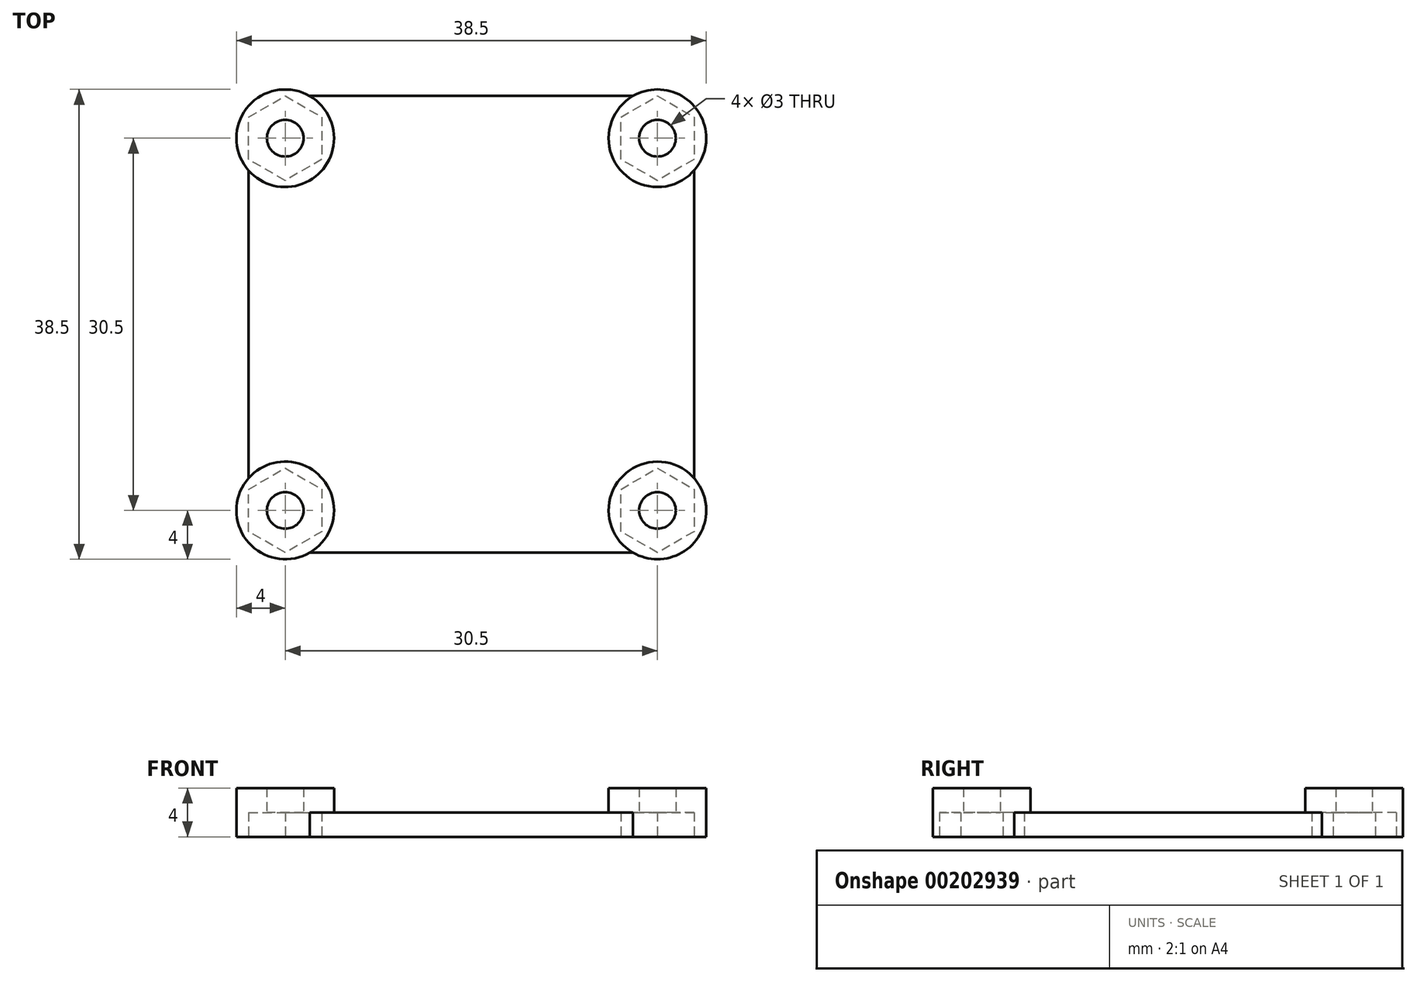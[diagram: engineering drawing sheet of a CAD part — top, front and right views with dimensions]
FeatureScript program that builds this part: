
annotation { "Feature Type Name" : "Feature", "Feature Type Description" : "" }
export const myFeature = defineFeature(function(context is Context, id is Id, definition is map)
    precondition{}
    {
        {
            var Q0;
            Q0=qCreatedBy(makeId("Top.planeOp"),FACE);
            var sketch = newSketch(context, id + "F0", { "sketchPlane" : qUnion([Q0])});
            skCircle(sketch, "E0", {"center": v(0, 0) * mm, "radius": 1.5 * mm});
            skCircle(sketch, "E1.0.1.0", {"center": v(0, 30.5) * mm, "radius": 1.5 * mm});
            skCircle(sketch, "E1.1.0.0", {"center": v(30.5, 0) * mm, "radius": 1.5 * mm});
            skCircle(sketch, "E1.1.1.0", {"center": v(30.5, 30.5) * mm, "radius": 1.5 * mm});
            skLineSegment(sketch, "E1.direction1", {"start": v(0, 0) * mm, "end": v(30.5, 0) * mm, "construction": true});
            skLineSegment(sketch, "E1.direction2", {"start": v(0, 0) * mm, "end": v(0, 30.5) * mm, "construction": true});
            skCircle(sketch, "E2", {"center": v(0, 0) * mm, "radius": 4 * mm});
            skCircle(sketch, "E3.0.1.0", {"center": v(0, 30.5) * mm, "radius": 4 * mm});
            skCircle(sketch, "E3.1.0.0", {"center": v(30.5, 0) * mm, "radius": 4 * mm});
            skCircle(sketch, "E3.1.1.0", {"center": v(30.5, 30.5) * mm, "radius": 4 * mm});
            skCircle(sketch, "E4.cCircle", {"center": v(0, 0) * mm, "radius": 3 * mm});
            skLineSegment(sketch, "E4.0", {"start": v(3, 1.73) * mm, "end": v(3, -1.73) * mm});
            skLineSegment(sketch, "E4.1", {"start": v(3, -1.73) * mm, "end": v(0, -3.46) * mm});
            skLineSegment(sketch, "E4.2", {"start": v(0, -3.46) * mm, "end": v(-3, -1.73) * mm});
            skLineSegment(sketch, "E4.3", {"start": v(-3, -1.73) * mm, "end": v(-3, 1.73) * mm});
            skLineSegment(sketch, "E4.4", {"start": v(-3, 1.73) * mm, "end": v(0, 3.46) * mm});
            skLineSegment(sketch, "E4.5", {"start": v(0, 3.46) * mm, "end": v(3, 1.73) * mm});
            skPoint(sketch, "E4.0.midPoint", {"position": v(3, 0) * mm});
            skLineSegment(sketch, "E5.0.1.0", {"start": v(0, 33.96) * mm, "end": v(3, 32.23) * mm});
            skLineSegment(sketch, "E5.0.1.1", {"start": v(3, 32.23) * mm, "end": v(3, 28.77) * mm});
            skLineSegment(sketch, "E5.0.1.2", {"start": v(3, 28.77) * mm, "end": v(0, 27.04) * mm});
            skLineSegment(sketch, "E5.0.1.3", {"start": v(0, 27.04) * mm, "end": v(-3, 28.77) * mm});
            skLineSegment(sketch, "E5.0.1.4", {"start": v(-3, 28.77) * mm, "end": v(-3, 32.23) * mm});
            skLineSegment(sketch, "E5.0.1.5", {"start": v(-3, 32.23) * mm, "end": v(0, 33.96) * mm});
            skLineSegment(sketch, "E5.1.0.0", {"start": v(30.5, 3.46) * mm, "end": v(33.5, 1.73) * mm});
            skLineSegment(sketch, "E5.1.0.1", {"start": v(33.5, 1.73) * mm, "end": v(33.5, -1.73) * mm});
            skLineSegment(sketch, "E5.1.0.2", {"start": v(33.5, -1.73) * mm, "end": v(30.5, -3.46) * mm});
            skLineSegment(sketch, "E5.1.0.3", {"start": v(30.5, -3.46) * mm, "end": v(27.5, -1.73) * mm});
            skLineSegment(sketch, "E5.1.0.4", {"start": v(27.5, -1.73) * mm, "end": v(27.5, 1.73) * mm});
            skLineSegment(sketch, "E5.1.0.5", {"start": v(27.5, 1.73) * mm, "end": v(30.5, 3.46) * mm});
            skLineSegment(sketch, "E5.1.1.0", {"start": v(30.5, 33.96) * mm, "end": v(33.5, 32.23) * mm});
            skLineSegment(sketch, "E5.1.1.1", {"start": v(33.5, 32.23) * mm, "end": v(33.5, 28.77) * mm});
            skLineSegment(sketch, "E5.1.1.2", {"start": v(33.5, 28.77) * mm, "end": v(30.5, 27.04) * mm});
            skLineSegment(sketch, "E5.1.1.3", {"start": v(30.5, 27.04) * mm, "end": v(27.5, 28.77) * mm});
            skLineSegment(sketch, "E5.1.1.4", {"start": v(27.5, 28.77) * mm, "end": v(27.5, 32.23) * mm});
            skLineSegment(sketch, "E5.1.1.5", {"start": v(27.5, 32.23) * mm, "end": v(30.5, 33.96) * mm});
            skLineSegment(sketch, "E5.direction1", {"start": v(0, 3.46) * mm, "end": v(30.5, 3.46) * mm, "construction": true});
            skLineSegment(sketch, "E5.direction2", {"start": v(0, 3.46) * mm, "end": v(0, 33.96) * mm, "construction": true});
            skLineSegment(sketch, "E6", {"start": v(33.5, 28.77) * mm, "end": v(33.5, 1.73) * mm});
            skLineSegment(sketch, "E7", {"start": v(-3, 1.73) * mm, "end": v(-3, 28.77) * mm});
            skLineSegment(sketch, "E8", {"start": v(30.5, -3.46) * mm, "end": v(0, -3.46) * mm});
            skLineSegment(sketch, "E9", {"start": v(30.5, 33.96) * mm, "end": v(0, 33.96) * mm});
            skSolve(sketch);
        }
        {
            var Q0;
            {var subQ6=sQuery(id+"F0.wireOp",EDGE,"E2");var subQ11=sQuery(id+"F0.wireOp",EDGE,"E7");var subQ12=makeQuery(id+"F0.imprint","INTERSECT",VERTEX,{"derivedFrom":[subQ6,subQ11]});Q0=makeQuery(id+"F0.imprint","IMPRINT",FACE,{"disambiguationData":[TD([[makeQuery(id+"F0.imprint","IMPRINT",EDGE,{"disambiguationData":[TD([[subQ12,1.0]])],"derivedFrom":subQ6}),-1.0]])]});}
            extrude(context, id + "F1", {"entities" : qUnion([Q0]), "depth" : 2 * mm});
        }
        {
            var Q0;
            {var subQ5=sQuery(id+"F0.wireOp",EDGE,"E5.0.1.0");Q0=makeQuery(id+"F0.imprint","IMPRINT",FACE,{"disambiguationData":[TD([[makeQuery(id+"F0.imprint","IMPRINT",EDGE,{"derivedFrom":subQ5}),1.0]])]});}
            var Q1;
            {var subQ1=sQuery(id+"F0.wireOp",EDGE,"E5.0.1.4");Q1=makeQuery(id+"F0.imprint","IMPRINT",FACE,{"disambiguationData":[TD([[makeQuery(id+"F0.imprint","IMPRINT",EDGE,{"derivedFrom":subQ1}),1.0]])]});}
            var Q2;
            {var subQ5=sQuery(id+"F0.wireOp",EDGE,"E7");var subQ14=sQuery(id+"F0.wireOp",EDGE,"E2");var subQ15=makeQuery(id+"F0.imprint","INTERSECT",VERTEX,{"derivedFrom":[subQ14,subQ5]});Q2=makeQuery(id+"F0.imprint","IMPRINT",FACE,{"disambiguationData":[TD([[makeQuery(id+"F0.imprint","IMPRINT",EDGE,{"disambiguationData":[TD([[subQ15,1.0]])],"derivedFrom":subQ14}),1.0]])]});}
            var Q3;
            {var subQ8=sQuery(id+"F0.wireOp",EDGE,"E7");var subQ9=sQuery(id+"F0.wireOp",EDGE,"E2");var subQ10=makeQuery(id+"F0.imprint","INTERSECT",VERTEX,{"derivedFrom":[subQ9,subQ8]});Q3=makeQuery(id+"F0.imprint","IMPRINT",FACE,{"disambiguationData":[TD([[makeQuery(id+"F0.imprint","IMPRINT",EDGE,{"disambiguationData":[TD([[subQ10,-1.0]])],"derivedFrom":subQ9}),1.0]])]});}
            var Q4;
            {var subQ0=sQuery(id+"F0.wireOp",EDGE,"E5.1.1.2");Q4=makeQuery(id+"F0.imprint","IMPRINT",FACE,{"disambiguationData":[TD([[makeQuery(id+"F0.imprint","IMPRINT",EDGE,{"derivedFrom":subQ0}),1.0]])]});}
            var Q5;
            {var subQ4=sQuery(id+"F0.wireOp",EDGE,"E5.1.1.0");Q5=makeQuery(id+"F0.imprint","IMPRINT",FACE,{"disambiguationData":[TD([[makeQuery(id+"F0.imprint","IMPRINT",EDGE,{"derivedFrom":subQ4}),1.0]])]});}
            var Q6;
            {var subQ1=sQuery(id+"F0.wireOp",EDGE,"E5.1.0.1");Q6=makeQuery(id+"F0.imprint","IMPRINT",FACE,{"disambiguationData":[TD([[makeQuery(id+"F0.imprint","IMPRINT",EDGE,{"derivedFrom":subQ1}),1.0]])]});}
            var Q7;
            {var subQ1=sQuery(id+"F0.wireOp",EDGE,"E5.1.0.0");Q7=makeQuery(id+"F0.imprint","IMPRINT",FACE,{"disambiguationData":[TD([[makeQuery(id+"F0.imprint","IMPRINT",EDGE,{"derivedFrom":subQ1}),1.0]])]});}
            extrude(context, id + "F2", {"entities" : qUnion([Q0, Q1, Q2, Q3, Q4, Q5, Q6, Q7]), "operationType" : NewBodyOperationType.ADD, "depth" : 4 * mm});
        }
        {
            var Q0;
            Q0=makeQuery(id+"F0.imprint","IMPRINT",FACE,{"disambiguationData":[TD([[makeQuery(id+"F0.imprint","IMPRINT",EDGE,{"derivedFrom":sQuery(id+"F0.wireOp",EDGE,"E0")}),-1.0]])]});
            var Q1;
            {var subQ5=sQuery(id+"F0.wireOp",EDGE,"E7");var subQ14=sQuery(id+"F0.wireOp",EDGE,"E2");var subQ15=makeQuery(id+"F0.imprint","INTERSECT",VERTEX,{"derivedFrom":[subQ14,subQ5]});Q1=makeQuery(id+"F0.imprint","IMPRINT",FACE,{"disambiguationData":[TD([[makeQuery(id+"F0.imprint","IMPRINT",EDGE,{"disambiguationData":[TD([[subQ15,1.0]])],"derivedFrom":subQ14}),1.0]])]});}
            var Q2;
            {var subQ0=sQuery(id+"F0.wireOp",EDGE,"E4.4");var subQ1=sQuery(id+"F0.wireOp",EDGE,"E4.cCircle");var subQ2=makeQuery(id+"F0.imprint","INTERSECT",VERTEX,{"derivedFrom":[subQ1,subQ0]});Q2=makeQuery(id+"F0.imprint","IMPRINT",FACE,{"disambiguationData":[TD([[makeQuery(id+"F0.imprint","IMPRINT",EDGE,{"disambiguationData":[TD([[subQ2,-1.0]])],"derivedFrom":subQ1}),-1.0]])]});}
            var Q3;
            {var subQ0=sQuery(id+"F0.wireOp",EDGE,"E4.5");var subQ1=sQuery(id+"F0.wireOp",EDGE,"E4.cCircle");var subQ2=makeQuery(id+"F0.imprint","INTERSECT",VERTEX,{"derivedFrom":[subQ1,subQ0]});Q3=makeQuery(id+"F0.imprint","IMPRINT",FACE,{"disambiguationData":[TD([[makeQuery(id+"F0.imprint","IMPRINT",EDGE,{"disambiguationData":[TD([[subQ2,-1.0]])],"derivedFrom":subQ1}),-1.0]])]});}
            var Q4;
            {var subQ0=sQuery(id+"F0.wireOp",EDGE,"E4.5");var subQ1=sQuery(id+"F0.wireOp",EDGE,"E4.cCircle");var subQ2=makeQuery(id+"F0.imprint","INTERSECT",VERTEX,{"derivedFrom":[subQ1,subQ0]});Q4=makeQuery(id+"F0.imprint","IMPRINT",FACE,{"disambiguationData":[TD([[makeQuery(id+"F0.imprint","IMPRINT",EDGE,{"disambiguationData":[TD([[subQ2,1.0]])],"derivedFrom":subQ1}),-1.0]])]});}
            var Q5;
            {var subQ0=sQuery(id+"F0.wireOp",EDGE,"E4.0");var subQ1=sQuery(id+"F0.wireOp",EDGE,"E4.cCircle");var subQ2=makeQuery(id+"F0.imprint","INTERSECT",VERTEX,{"derivedFrom":[subQ1,subQ0]});Q5=makeQuery(id+"F0.imprint","IMPRINT",FACE,{"disambiguationData":[TD([[makeQuery(id+"F0.imprint","IMPRINT",EDGE,{"disambiguationData":[TD([[subQ2,1.0]])],"derivedFrom":subQ1}),-1.0]])]});}
            var Q6;
            {var subQ0=sQuery(id+"F0.wireOp",EDGE,"E4.3");var subQ1=sQuery(id+"F0.wireOp",EDGE,"E4.cCircle");var subQ2=makeQuery(id+"F0.imprint","INTERSECT",VERTEX,{"derivedFrom":[subQ1,subQ0]});Q6=makeQuery(id+"F0.imprint","IMPRINT",FACE,{"disambiguationData":[TD([[makeQuery(id+"F0.imprint","IMPRINT",EDGE,{"disambiguationData":[TD([[subQ2,-1.0]])],"derivedFrom":subQ1}),-1.0]])]});}
            var Q7;
            {var subQ8=sQuery(id+"F0.wireOp",EDGE,"E7");var subQ9=sQuery(id+"F0.wireOp",EDGE,"E2");var subQ10=makeQuery(id+"F0.imprint","INTERSECT",VERTEX,{"derivedFrom":[subQ9,subQ8]});Q7=makeQuery(id+"F0.imprint","IMPRINT",FACE,{"disambiguationData":[TD([[makeQuery(id+"F0.imprint","IMPRINT",EDGE,{"disambiguationData":[TD([[subQ10,-1.0]])],"derivedFrom":subQ9}),1.0]])]});}
            var Q8;
            {var subQ0=sQuery(id+"F0.wireOp",EDGE,"E4.2");var subQ1=sQuery(id+"F0.wireOp",EDGE,"E4.cCircle");var subQ2=makeQuery(id+"F0.imprint","INTERSECT",VERTEX,{"derivedFrom":[subQ1,subQ0]});Q8=makeQuery(id+"F0.imprint","IMPRINT",FACE,{"disambiguationData":[TD([[makeQuery(id+"F0.imprint","IMPRINT",EDGE,{"disambiguationData":[TD([[subQ2,-1.0]])],"derivedFrom":subQ1}),-1.0]])]});}
            var Q9;
            Q9=makeQuery(id+"F0.imprint","IMPRINT",FACE,{"disambiguationData":[TD([[makeQuery(id+"F0.imprint","IMPRINT",EDGE,{"derivedFrom":sQuery(id+"F0.wireOp",EDGE,"E1.1.0.0")}),-1.0]])]});
            var Q10;
            {var subQ1=sQuery(id+"F0.wireOp",EDGE,"E5.1.0.0");Q10=makeQuery(id+"F0.imprint","IMPRINT",FACE,{"disambiguationData":[TD([[makeQuery(id+"F0.imprint","IMPRINT",EDGE,{"derivedFrom":subQ1}),1.0]])]});}
            var Q11;
            {var subQ1=sQuery(id+"F0.wireOp",EDGE,"E5.1.0.1");Q11=makeQuery(id+"F0.imprint","IMPRINT",FACE,{"disambiguationData":[TD([[makeQuery(id+"F0.imprint","IMPRINT",EDGE,{"derivedFrom":subQ1}),1.0]])]});}
            var Q12;
            {var subQ4=sQuery(id+"F0.wireOp",EDGE,"E5.1.1.0");Q12=makeQuery(id+"F0.imprint","IMPRINT",FACE,{"disambiguationData":[TD([[makeQuery(id+"F0.imprint","IMPRINT",EDGE,{"derivedFrom":subQ4}),1.0]])]});}
            var Q13;
            Q13=makeQuery(id+"F0.imprint","IMPRINT",FACE,{"disambiguationData":[TD([[makeQuery(id+"F0.imprint","IMPRINT",EDGE,{"derivedFrom":sQuery(id+"F0.wireOp",EDGE,"E1.1.1.0")}),-1.0]])]});
            var Q14;
            {var subQ0=sQuery(id+"F0.wireOp",EDGE,"E5.1.1.2");Q14=makeQuery(id+"F0.imprint","IMPRINT",FACE,{"disambiguationData":[TD([[makeQuery(id+"F0.imprint","IMPRINT",EDGE,{"derivedFrom":subQ0}),1.0]])]});}
            var Q15;
            {var subQ1=sQuery(id+"F0.wireOp",EDGE,"E5.0.1.4");Q15=makeQuery(id+"F0.imprint","IMPRINT",FACE,{"disambiguationData":[TD([[makeQuery(id+"F0.imprint","IMPRINT",EDGE,{"derivedFrom":subQ1}),1.0]])]});}
            var Q16;
            Q16=makeQuery(id+"F0.imprint","IMPRINT",FACE,{"disambiguationData":[TD([[makeQuery(id+"F0.imprint","IMPRINT",EDGE,{"derivedFrom":sQuery(id+"F0.wireOp",EDGE,"E1.0.1.0")}),-1.0]])]});
            var Q17;
            {var subQ5=sQuery(id+"F0.wireOp",EDGE,"E5.0.1.0");Q17=makeQuery(id+"F0.imprint","IMPRINT",FACE,{"disambiguationData":[TD([[makeQuery(id+"F0.imprint","IMPRINT",EDGE,{"derivedFrom":subQ5}),1.0]])]});}
            extrude(context, id + "F3", {"entities" : qUnion([Q0, Q1, Q2, Q3, Q4, Q5, Q6, Q7, Q8, Q9, Q10, Q11, Q12, Q13, Q14, Q15, Q16, Q17]), "operationType" : NewBodyOperationType.ADD, "depth" : 4 * mm});
        }
        {
            var Q0;
            Q0=makeQuery(id+"F0.imprint","IMPRINT",FACE,{"disambiguationData":[TD([[makeQuery(id+"F0.imprint","IMPRINT",EDGE,{"derivedFrom":sQuery(id+"F0.wireOp",EDGE,"E1.0.1.0")}),-1.0]])]});
            var Q1;
            Q1=makeQuery(id+"F0.imprint","IMPRINT",FACE,{"disambiguationData":[TD([[makeQuery(id+"F0.imprint","IMPRINT",EDGE,{"derivedFrom":sQuery(id+"F0.wireOp",EDGE,"E1.1.1.0")}),-1.0]])]});
            var Q2;
            Q2=makeQuery(id+"F0.imprint","IMPRINT",FACE,{"disambiguationData":[TD([[makeQuery(id+"F0.imprint","IMPRINT",EDGE,{"derivedFrom":sQuery(id+"F0.wireOp",EDGE,"E1.1.0.0")}),-1.0]])]});
            var Q3;
            Q3=makeQuery(id+"F0.imprint","IMPRINT",FACE,{"disambiguationData":[TD([[makeQuery(id+"F0.imprint","IMPRINT",EDGE,{"derivedFrom":sQuery(id+"F0.wireOp",EDGE,"E0")}),-1.0]])]});
            var Q4;
            {var subQ0=sQuery(id+"F0.wireOp",EDGE,"E4.4");var subQ1=sQuery(id+"F0.wireOp",EDGE,"E4.cCircle");var subQ2=makeQuery(id+"F0.imprint","INTERSECT",VERTEX,{"derivedFrom":[subQ1,subQ0]});Q4=makeQuery(id+"F0.imprint","IMPRINT",FACE,{"disambiguationData":[TD([[makeQuery(id+"F0.imprint","IMPRINT",EDGE,{"disambiguationData":[TD([[subQ2,-1.0]])],"derivedFrom":subQ1}),-1.0]])]});}
            var Q5;
            {var subQ0=sQuery(id+"F0.wireOp",EDGE,"E4.3");var subQ1=sQuery(id+"F0.wireOp",EDGE,"E4.cCircle");var subQ2=makeQuery(id+"F0.imprint","INTERSECT",VERTEX,{"derivedFrom":[subQ1,subQ0]});Q5=makeQuery(id+"F0.imprint","IMPRINT",FACE,{"disambiguationData":[TD([[makeQuery(id+"F0.imprint","IMPRINT",EDGE,{"disambiguationData":[TD([[subQ2,-1.0]])],"derivedFrom":subQ1}),-1.0]])]});}
            var Q6;
            {var subQ0=sQuery(id+"F0.wireOp",EDGE,"E4.0");var subQ1=sQuery(id+"F0.wireOp",EDGE,"E4.cCircle");var subQ2=makeQuery(id+"F0.imprint","INTERSECT",VERTEX,{"derivedFrom":[subQ1,subQ0]});Q6=makeQuery(id+"F0.imprint","IMPRINT",FACE,{"disambiguationData":[TD([[makeQuery(id+"F0.imprint","IMPRINT",EDGE,{"disambiguationData":[TD([[subQ2,1.0]])],"derivedFrom":subQ1}),-1.0]])]});}
            var Q7;
            {var subQ0=sQuery(id+"F0.wireOp",EDGE,"E4.5");var subQ1=sQuery(id+"F0.wireOp",EDGE,"E4.cCircle");var subQ2=makeQuery(id+"F0.imprint","INTERSECT",VERTEX,{"derivedFrom":[subQ1,subQ0]});Q7=makeQuery(id+"F0.imprint","IMPRINT",FACE,{"disambiguationData":[TD([[makeQuery(id+"F0.imprint","IMPRINT",EDGE,{"disambiguationData":[TD([[subQ2,1.0]])],"derivedFrom":subQ1}),-1.0]])]});}
            var Q8;
            {var subQ0=sQuery(id+"F0.wireOp",EDGE,"E4.5");var subQ1=sQuery(id+"F0.wireOp",EDGE,"E4.cCircle");var subQ2=makeQuery(id+"F0.imprint","INTERSECT",VERTEX,{"derivedFrom":[subQ1,subQ0]});Q8=makeQuery(id+"F0.imprint","IMPRINT",FACE,{"disambiguationData":[TD([[makeQuery(id+"F0.imprint","IMPRINT",EDGE,{"disambiguationData":[TD([[subQ2,-1.0]])],"derivedFrom":subQ1}),-1.0]])]});}
            var Q9;
            {var subQ0=sQuery(id+"F0.wireOp",EDGE,"E4.2");var subQ1=sQuery(id+"F0.wireOp",EDGE,"E4.cCircle");var subQ2=makeQuery(id+"F0.imprint","INTERSECT",VERTEX,{"derivedFrom":[subQ1,subQ0]});Q9=makeQuery(id+"F0.imprint","IMPRINT",FACE,{"disambiguationData":[TD([[makeQuery(id+"F0.imprint","IMPRINT",EDGE,{"disambiguationData":[TD([[subQ2,-1.0]])],"derivedFrom":subQ1}),-1.0]])]});}
            extrude(context, id + "F4", {"entities" : qUnion([Q0, Q1, Q2, Q3, Q4, Q5, Q6, Q7, Q8, Q9]), "operationType" : NewBodyOperationType.REMOVE, "depth" : 2 * mm});
        }
    });
